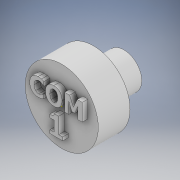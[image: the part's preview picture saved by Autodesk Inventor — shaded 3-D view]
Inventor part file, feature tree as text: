
AUTODESK INVENTOR PART (.ipt)
format: ipt  version: 2022 (Build 260153000, 153)  size: 210,432 bytes
history: native  units: in
note: dims shown in document units (in); Inventor stores cm internally (conversion verified against a paired STEP export)
features: sketch x3, extrude x3
ambient origin geometry x8: Origin, YZ Plane, XZ Plane, XY Plane, X Axis, Y Axis, Z Axis, Center Point
bodies: Solid1 (feature_tree)
feature tree (6):
  sketch  "Sketch1"  dims[d0=0.4898in d1=0.0185in]
  extrude  "Extrusion1"  Depth=0.0185in
  extrude  "Extrusion2"  Depth=0.1969in TaperAngle=0.0deg
  sketch  "Sketch2"  dims[d2=0.1969in d3=0.0in d4=0.189in d5=0.0in]
  extrude  "Extrusion3"  [1 undecoded]
  sketch  "Sketch3"  dims[d6=0.0354in d7=0.0in]
note: 1 required parameter value undecoded (feature->parameter linkage not recoverable at this tier; creation-order binding heuristic only, values carry confidence <= 0.55)
